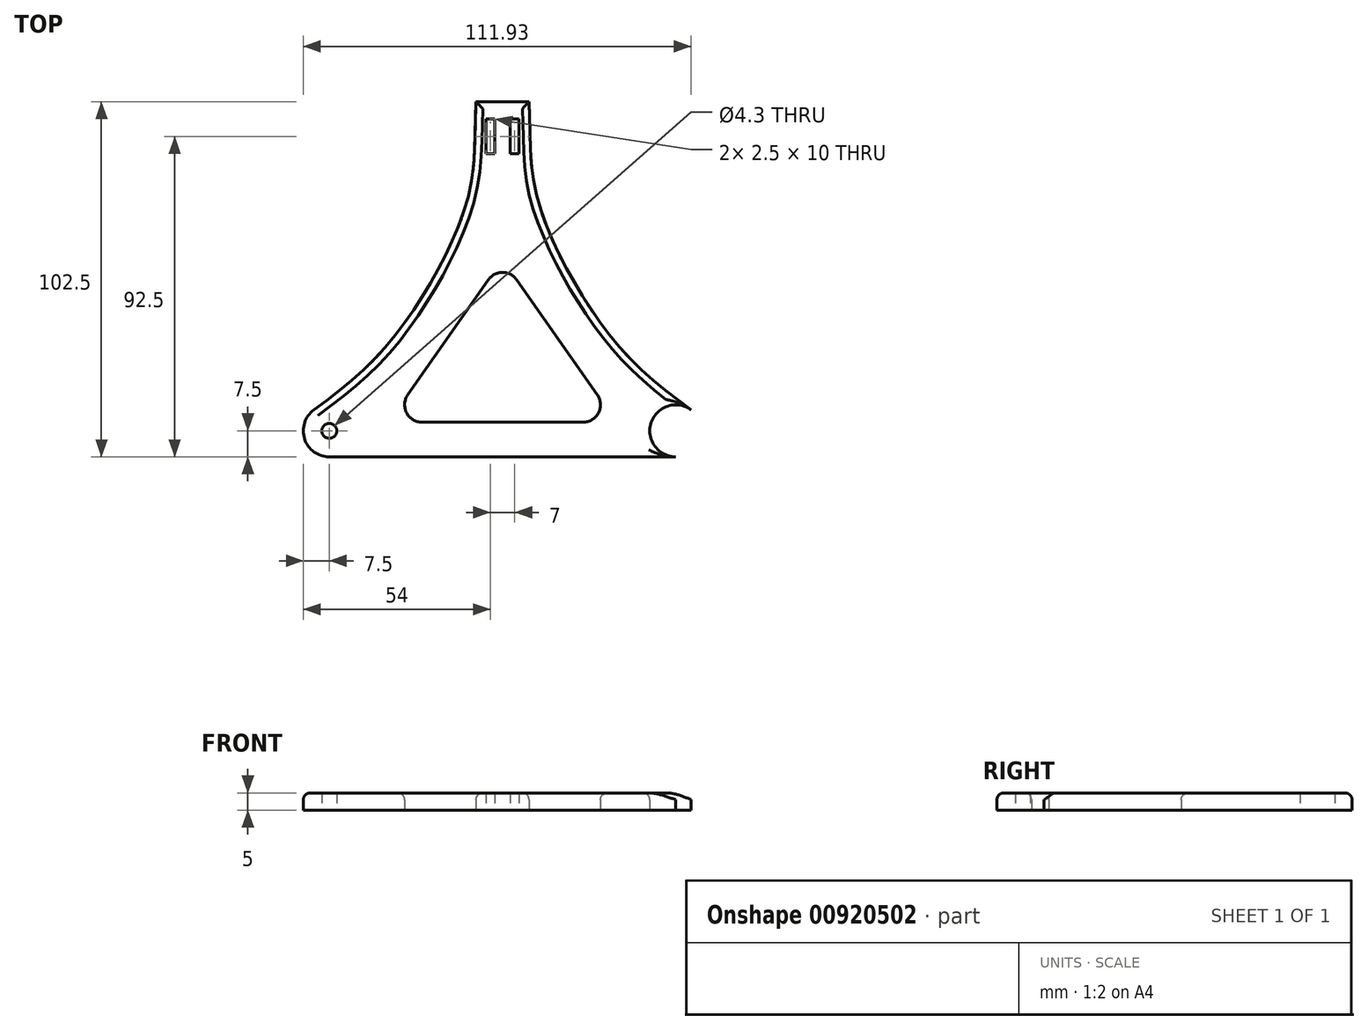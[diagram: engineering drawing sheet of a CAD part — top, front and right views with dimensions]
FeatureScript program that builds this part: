
annotation { "Feature Type Name" : "Feature", "Feature Type Description" : "" }
export const myFeature = defineFeature(function(context is Context, id is Id, definition is map)
    precondition{}
    {
        {
            var Q0;
            Q0=qCreatedBy(makeId("Top.planeOp"),FACE);
            var sketch = newSketch(context, id + "F0", { "sketchPlane" : qUnion([Q0])});
            skLineSegment(sketch, "E0", {"start": v(0, 0) * mm, "end": v(0, -50) * mm, "construction": true});
            skLineSegment(sketch, "E1", {"start": v(0, 0) * mm, "end": v(0, 45) * mm, "construction": true});
            skLineSegment(sketch, "E2", {"start": v(0, -50) * mm, "end": v(-50, -50) * mm, "construction": true});
            skCircle(sketch, "E3", {"center": v(-50, -50) * mm, "radius": 7.5 * mm});
            skLineSegment(sketch, "E4.MirrorCS", {"start": v(0, -50) * mm, "end": v(50, -50) * mm, "construction": true});
            skCircle(sketch, "E5.MirrorC", {"center": v(50, -50) * mm, "radius": 7.5 * mm});
            skLineSegment(sketch, "E6", {"start": v(50, -57.5) * mm, "end": v(-50, -57.5) * mm});
            skLineSegment(sketch, "E7", {"start": v(0, 45) * mm, "end": v(7.65, 45) * mm});
            skFitSpline(sketch, "E8", {"points": [v(7.65, 45) * mm, v(10.6, 15.08) * mm, v(31.4, -22.96) * mm, v(54.43, -43.95) * mm], "startDerivative": vector(4.77, -126.08) * mm, "endDerivative": vector(78.99, -58.31) * mm});
            skFitSpline(sketch, "E9.MirrorCS", {"points": [v(-7.65, 45) * mm, v(-10.6, 15.08) * mm, v(-31.4, -22.96) * mm, v(-54.43, -43.95) * mm], "startDerivative": vector(-4.77, -126.08) * mm, "endDerivative": vector(-78.99, -58.31) * mm});
            skLineSegment(sketch, "E10.MirrorCS", {"start": v(0, 45) * mm, "end": v(-7.65, 45) * mm});
            skLineSegment(sketch, "E11", {"start": v(0, -47.5) * mm, "end": v(23.26, -47.5) * mm});
            skCircle(sketch, "E12", {"center": v(0, -9.28) * mm, "radius": 5 * mm});
            skLineSegment(sketch, "E13", {"start": v(0, -42.5) * mm, "end": v(23.26, -42.5) * mm, "construction": true});
            skCircle(sketch, "E14", {"center": v(23.26, -42.5) * mm, "radius": 5 * mm});
            skLineSegment(sketch, "E15", {"start": v(4.1, -6.42) * mm, "end": v(27.35, -39.63) * mm});
            skLineSegment(sketch, "E16.MirrorCS", {"start": v(0, -47.5) * mm, "end": v(-23.26, -47.5) * mm});
            skCircle(sketch, "E17.MirrorC", {"center": v(-23.26, -42.5) * mm, "radius": 5 * mm});
            skLineSegment(sketch, "E18.MirrorCS", {"start": v(-4.1, -6.42) * mm, "end": v(-27.35, -39.63) * mm});
            skLineSegment(sketch, "E19", {"start": v(23.26, -42.5) * mm, "end": v(0, -9.28) * mm, "construction": true});
            skLineSegment(sketch, "E20.bottom", {"start": v(-2.25, 30) * mm, "end": v(-4.75, 30) * mm});
            skLineSegment(sketch, "E20.top", {"start": v(-2.25, 40) * mm, "end": v(-4.75, 40) * mm});
            skLineSegment(sketch, "E20.left", {"start": v(-2.25, 30) * mm, "end": v(-2.25, 40) * mm});
            skLineSegment(sketch, "E20.right", {"start": v(-4.75, 30) * mm, "end": v(-4.75, 40) * mm});
            skPoint(sketch, "E20.middle", {"position": v(-3.5, 35) * mm});
            skLineSegment(sketch, "E21.MirrorCS", {"start": v(2.25, 30) * mm, "end": v(2.25, 40) * mm});
            skPoint(sketch, "E22.MirrorP", {"position": v(3.5, 35) * mm});
            skLineSegment(sketch, "E23.MirrorCS", {"start": v(4.75, 30) * mm, "end": v(4.75, 40) * mm});
            skLineSegment(sketch, "E24.MirrorCS", {"start": v(2.25, 30) * mm, "end": v(4.75, 30) * mm});
            skLineSegment(sketch, "E25.MirrorCS", {"start": v(2.25, 40) * mm, "end": v(4.75, 40) * mm});
            skSolve(sketch);
        }
        {
            var Q0;
            {var subQ0=sQuery(id+"F0.wireOp",EDGE,"E6");Q0=makeQuery(id+"F0.imprint","IMPRINT",FACE,{"disambiguationData":[TD([[makeQuery(id+"F0.imprint","IMPRINT",EDGE,{"derivedFrom":subQ0}),-1.0]])]});}
            var Q1;
            {var subQ0=sQuery(id+"F0.wireOp",EDGE,"E3");var subQ1=makeQuery(id+"F0.imprint","INTERSECT",VERTEX,{"derivedFrom":[subQ0,sQuery(id+"F0.wireOp",EDGE,"E6")]});Q1=makeQuery(id+"F0.imprint","IMPRINT",FACE,{"disambiguationData":[TD([[makeQuery(id+"F0.imprint","IMPRINT",EDGE,{"disambiguationData":[TD([[subQ1,1.0]])],"derivedFrom":subQ0}),1.0]])]});}
            var Q2;
            {var subQ0=sQuery(id+"F0.wireOp",EDGE,"E5.MirrorC");var subQ1=makeQuery(id+"F0.imprint","INTERSECT",VERTEX,{"derivedFrom":[subQ0,sQuery(id+"F0.wireOp",EDGE,"E6")]});Q2=makeQuery(id+"F0.imprint","IMPRINT",FACE,{"disambiguationData":[TD([[makeQuery(id+"F0.imprint","IMPRINT",EDGE,{"disambiguationData":[TD([[subQ1,1.0]])],"derivedFrom":subQ0}),-1.0]])]});}
            extrude(context, id + "F1", {"entities" : qUnion([Q0, Q1, Q2]), "depth" : 5 * mm, "offsetDistance" : 25 * mm});
        }
        {
            var Q0;
            Q0=sQuery(id+"F0.wireOp",VERTEX,"E2.end");
            var Q1;
            Q1=sQuery(id+"F0.wireOp",VERTEX,"E4.MirrorCS.end");
            var Q2;
            Q2=makeQuery(id+"F1.opExtrude","SWEPT_BODY",BODY,{"disambiguationData":[OSD([sQuery(id+"F0.wireOp",EDGE,"E3"),sQuery(id+"F0.wireOp",EDGE,"E5.MirrorC"),sQuery(id+"F0.wireOp",EDGE,"E6"),sQuery(id+"F0.wireOp",EDGE,"E7"),sQuery(id+"F0.wireOp",EDGE,"E8"),sQuery(id+"F0.wireOp",EDGE,"E9.MirrorCS"),sQuery(id+"F0.wireOp",EDGE,"E10.MirrorCS")])]});
            hole(context, id + "F2", {"style" : HoleStyle.SIMPLE, "endStyle" : HoleEndStyle.BLIND, "oppositeDirection" : true, "holeDiameter" : 4.3 * mm, "majorDiameter" : 5 * mm, "holeDepth" : 100 * mm, "isTappedThrough" : true, "tappedDepth" : 12 * mm, "tapClearance" : 3, "locations" : qUnion([Q0, Q1]), "scope" : qUnion([Q2])});
        }
        {
            var Q0;
            Q0=makeQuery(id+"F1.opExtrude","CAP_EDGE",EDGE,{"disambiguationData":[OSD([sQuery(id+"F0.wireOp",EDGE,"E3")])],"isStart":false});
            var Q1;
            Q1=makeQuery(id+"F1.opExtrude","CAP_EDGE",EDGE,{"disambiguationData":[OSD([sQuery(id+"F0.wireOp",EDGE,"E6")])],"isStart":false});
            var Q2;
            Q2=makeQuery(id+"F1.opExtrude","CAP_EDGE",EDGE,{"disambiguationData":[OSD([sQuery(id+"F0.wireOp",EDGE,"E9.MirrorCS")])],"isStart":false});
            var Q3;
            Q3=makeQuery(id+"F1.opExtrude","CAP_EDGE",EDGE,{"disambiguationData":[OSD([sQuery(id+"F0.wireOp",EDGE,"E5.MirrorC")])],"isStart":false});
            var Q4;
            Q4=makeQuery(id+"F1.opExtrude","CAP_EDGE",EDGE,{"disambiguationData":[OSD([sQuery(id+"F0.wireOp",EDGE,"E8")])],"isStart":false});
            var Q5;
            Q5=makeQuery(id+"F1.opExtrude","CAP_EDGE",EDGE,{"disambiguationData":[OSD([sQuery(id+"F0.wireOp",EDGE,"E7"),sQuery(id+"F0.wireOp",EDGE,"E10.MirrorCS")])],"isStart":false});
            var Q6;
            Q6=makeQuery(id+"F1.opExtrude","CAP_EDGE",EDGE,{"disambiguationData":[OSD([sQuery(id+"F0.wireOp",EDGE,"E11"),sQuery(id+"F0.wireOp",EDGE,"E16.MirrorCS")])],"isStart":false});
            fillet(context, id + "F3", {"entities" : qUnion([Q0, Q1, Q2, Q3, Q4, Q5, Q6]), "radius" : 2 * mm, "tangentPropagation" : true, "allowEdgeOverflow" : false});
        }
    });
